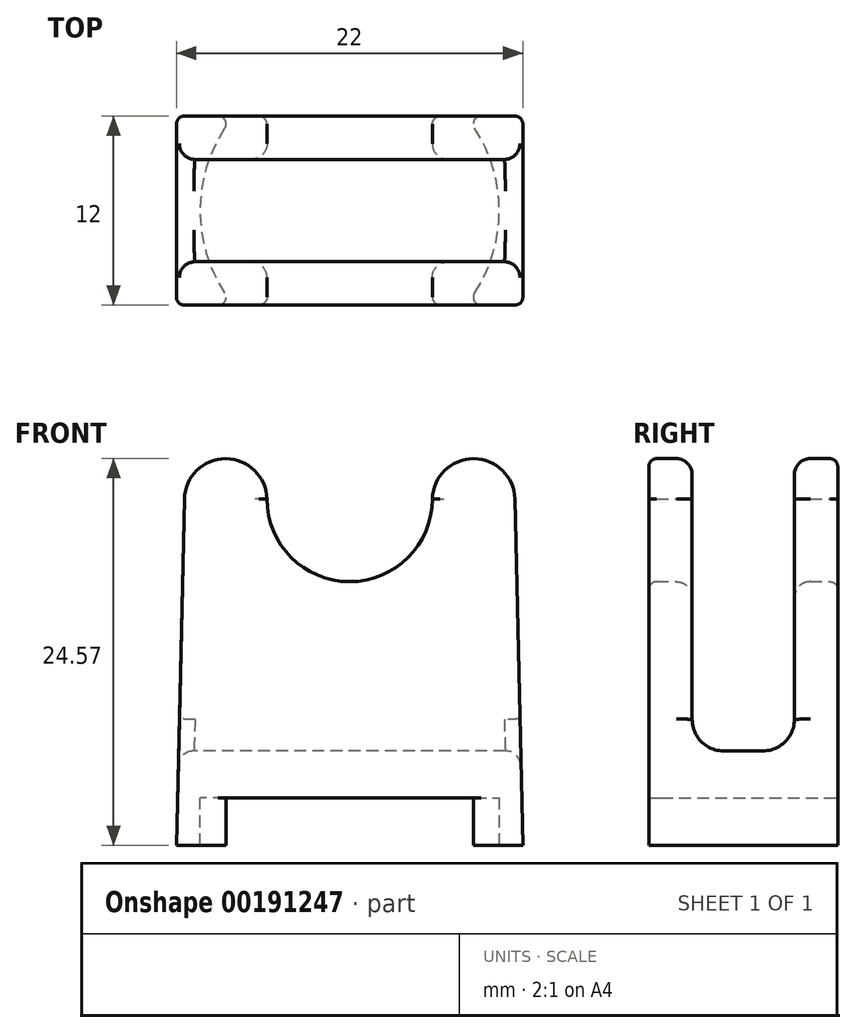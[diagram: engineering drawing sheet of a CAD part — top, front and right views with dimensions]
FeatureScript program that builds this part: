
annotation { "Feature Type Name" : "Feature", "Feature Type Description" : "" }
export const myFeature = defineFeature(function(context is Context, id is Id, definition is map)
    precondition{}
    {
        {
            var Q0;
            Q0=qCreatedBy(makeId("Front.planeOp"),FACE);
            var sketch = newSketch(context, id + "F0", { "sketchPlane" : qUnion([Q0])});
            skLineSegment(sketch, "E0", {"start": v(0, -3) * mm, "end": v(-11, -3) * mm});
            skLineSegment(sketch, "E1", {"start": v(-11, -3) * mm, "end": v(-10.5, 19) * mm});
            skLineSegment(sketch, "E2", {"start": v(-10.5, 19) * mm, "end": v(0, 19) * mm, "construction": true});
            skArc(sketch, "E3", {"start": v(-5.25, 19) * mm, "mid": v(0, 13.75) * mm, "end": v(5.25, 19) * mm});
            skArc(sketch, "E4", {"start": v(-10.5, 19) * mm, "mid": v(-7.87, 21.57) * mm, "end": v(-5.25, 19) * mm});
            skArc(sketch, "E5.MirrorCS", {"start": v(10.5, 19) * mm, "mid": v(7.87, 21.57) * mm, "end": v(5.25, 19) * mm});
            skLineSegment(sketch, "E6.MirrorCS", {"start": v(11, -3) * mm, "end": v(10.5, 19) * mm});
            skLineSegment(sketch, "E7.MirrorCS", {"start": v(0, -3) * mm, "end": v(11, -3) * mm});
            skSolve(sketch);
        }
        {
            var Q0;
            Q0=makeQuery(id+"F0.imprint","IMPRINT",FACE,{"disambiguationData":[TD([[makeQuery(id+"F0.imprint","IMPRINT",EDGE,{"derivedFrom":sQuery(id+"F0.wireOp",EDGE,"E0")}),-1.0]])]});
            extrude(context, id + "F1", {"entities" : qUnion([Q0]), "endBound" : BoundingType.SYMMETRIC, "depth" : 12 * mm});
        }
        {
            var Q0;
            Q0=qCreatedBy(makeId("Top.planeOp"),FACE);
            var sketch = newSketch(context, id + "F2", { "sketchPlane" : qUnion([Q0])});
            skCircle(sketch, "E8", {"center": v(0, 0) * mm, "radius": 9.5 * mm});
            skSolve(sketch);
        }
        {
            var Q0;
            Q0 = qSketchRegion(id + "F2", true);
            extrude(context, id + "F3", {"entities" : qUnion([Q0]), "operationType" : NewBodyOperationType.REMOVE, "oppositeDirection" : true, "depth" : 3 * mm});
        }
        {
            var Q0;
            Q0=qCreatedBy(makeId("Right.planeOp"),FACE);
            var sketch = newSketch(context, id + "F4", { "sketchPlane" : qUnion([Q0])});
            skLineSegment(sketch, "E9", {"start": v(0, 0) * mm, "end": v(0, 19) * mm, "construction": true});
            skLineSegment(sketch, "E10.bottom", {"start": v(3.25, 3) * mm, "end": v(-3.25, 3) * mm});
            skLineSegment(sketch, "E10.top", {"start": v(3.25, 35) * mm, "end": v(-3.25, 35) * mm});
            skLineSegment(sketch, "E10.left", {"start": v(3.25, 3) * mm, "end": v(3.25, 35) * mm});
            skLineSegment(sketch, "E10.right", {"start": v(-3.25, 3) * mm, "end": v(-3.25, 35) * mm});
            skPoint(sketch, "E10.middle", {"position": v(0, 19) * mm});
            skSolve(sketch);
        }
        {
            var Q0;
            Q0 = qSketchRegion(id + "F4", true);
            extrude(context, id + "F5", {"entities" : qUnion([Q0]), "operationType" : NewBodyOperationType.REMOVE, "endBound" : BoundingType.SYMMETRIC, "depth" : 22 * mm});
        }
        {
            var Q0;
            Q0=makeQuery(id+"F5.boolean.opBoolean","COPY",EDGE,{"derivedFrom":makeQuery(id+"F5.opExtrude","SWEPT_EDGE",EDGE,{"disambiguationData":[OSD([sQuery(id+"F4.wireOp",EDGE,"E10.bottom"),sQuery(id+"F4.wireOp",EDGE,"E10.left")])]})});
            var Q1;
            Q1=makeQuery(id+"F5.boolean.opBoolean","COPY",EDGE,{"derivedFrom":makeQuery(id+"F5.opExtrude","SWEPT_EDGE",EDGE,{"disambiguationData":[OSD([sQuery(id+"F4.wireOp",EDGE,"E10.bottom"),sQuery(id+"F4.wireOp",EDGE,"E10.right")])]})});
            fillet(context, id + "F6", {"entities" : qUnion([Q0, Q1]), "radius" : 2 * mm, "tangentPropagation" : true, "allowEdgeOverflow" : false});
        }
        {
            var Q0;
            Q0=makeQuery(id+"F5.boolean.opBoolean","INTERSECT",EDGE,{"derivedFrom":[makeQuery(id+"F1.opExtrude","SWEPT_FACE",FACE,{"disambiguationData":[OSD([sQuery(id+"F0.wireOp",EDGE,"E3")])]}),makeQuery(id+"F5.opExtrude","SWEPT_FACE",FACE,{"disambiguationData":[OSD([sQuery(id+"F4.wireOp",EDGE,"E10.left")])]})]});
            var Q1;
            Q1=makeQuery(id+"F5.boolean.opBoolean","INTERSECT",EDGE,{"derivedFrom":[makeQuery(id+"F1.opExtrude","SWEPT_FACE",FACE,{"disambiguationData":[OSD([sQuery(id+"F0.wireOp",EDGE,"E4")])]}),makeQuery(id+"F5.opExtrude","SWEPT_FACE",FACE,{"disambiguationData":[OSD([sQuery(id+"F4.wireOp",EDGE,"E10.left")])]})]});
            var Q2;
            Q2=makeQuery(id+"F5.boolean.opBoolean","INTERSECT",EDGE,{"derivedFrom":[makeQuery(id+"F1.opExtrude","SWEPT_FACE",FACE,{"disambiguationData":[OSD([sQuery(id+"F0.wireOp",EDGE,"E5.MirrorCS")])]}),makeQuery(id+"F5.opExtrude","SWEPT_FACE",FACE,{"disambiguationData":[OSD([sQuery(id+"F4.wireOp",EDGE,"E10.left")])]})]});
            var Q3;
            Q3=makeQuery(id+"F5.boolean.opBoolean","INTERSECT",EDGE,{"derivedFrom":[makeQuery(id+"F1.opExtrude","SWEPT_FACE",FACE,{"disambiguationData":[OSD([sQuery(id+"F0.wireOp",EDGE,"E1")])]}),makeQuery(id+"F5.opExtrude","SWEPT_FACE",FACE,{"disambiguationData":[OSD([sQuery(id+"F4.wireOp",EDGE,"E10.left")])]})]});
            var Q4;
            Q4=makeQuery(id+"F6.opFillet","BLEND_EDGE",EDGE,{"blendedFrom":[makeQuery(id+"F5.boolean.opBoolean","COPY",EDGE,{"derivedFrom":makeQuery(id+"F5.opExtrude","SWEPT_EDGE",EDGE,{"disambiguationData":[OSD([sQuery(id+"F4.wireOp",EDGE,"E10.bottom"),sQuery(id+"F4.wireOp",EDGE,"E10.left")])]})}),makeQuery(id+"F1.opExtrude","SWEPT_FACE",FACE,{"disambiguationData":[OSD([sQuery(id+"F0.wireOp",EDGE,"E1")])]})],"blendedInto":[makeQuery(id+"F1.opExtrude","SWEPT_FACE",FACE,{"disambiguationData":[OSD([sQuery(id+"F0.wireOp",EDGE,"E1")])]})]});
            var Q5;
            Q5=makeQuery(id+"F5.boolean.opBoolean","INTERSECT",EDGE,{"derivedFrom":[makeQuery(id+"F1.opExtrude","SWEPT_FACE",FACE,{"disambiguationData":[OSD([sQuery(id+"F0.wireOp",EDGE,"E1")])]}),makeQuery(id+"F5.opExtrude","SWEPT_FACE",FACE,{"disambiguationData":[OSD([sQuery(id+"F4.wireOp",EDGE,"E10.bottom")])]})]});
            var Q6;
            Q6=makeQuery(id+"F5.boolean.opBoolean","INTERSECT",EDGE,{"derivedFrom":[makeQuery(id+"F1.opExtrude","SWEPT_FACE",FACE,{"disambiguationData":[OSD([sQuery(id+"F0.wireOp",EDGE,"E1")])]}),makeQuery(id+"F5.opExtrude","SWEPT_FACE",FACE,{"disambiguationData":[OSD([sQuery(id+"F4.wireOp",EDGE,"E10.right")])]})]});
            var Q7;
            Q7=makeQuery(id+"F6.opFillet","BLEND_EDGE",EDGE,{"blendedFrom":[makeQuery(id+"F5.boolean.opBoolean","COPY",EDGE,{"derivedFrom":makeQuery(id+"F5.opExtrude","SWEPT_EDGE",EDGE,{"disambiguationData":[OSD([sQuery(id+"F4.wireOp",EDGE,"E10.bottom"),sQuery(id+"F4.wireOp",EDGE,"E10.right")])]})}),makeQuery(id+"F1.opExtrude","SWEPT_FACE",FACE,{"disambiguationData":[OSD([sQuery(id+"F0.wireOp",EDGE,"E1")])]})],"blendedInto":[makeQuery(id+"F1.opExtrude","SWEPT_FACE",FACE,{"disambiguationData":[OSD([sQuery(id+"F0.wireOp",EDGE,"E1")])]})]});
            var Q8;
            Q8=makeQuery(id+"F5.boolean.opBoolean","INTERSECT",EDGE,{"derivedFrom":[makeQuery(id+"F1.opExtrude","SWEPT_FACE",FACE,{"disambiguationData":[OSD([sQuery(id+"F0.wireOp",EDGE,"E4")])]}),makeQuery(id+"F5.opExtrude","SWEPT_FACE",FACE,{"disambiguationData":[OSD([sQuery(id+"F4.wireOp",EDGE,"E10.right")])]})]});
            var Q9;
            Q9=makeQuery(id+"F5.boolean.opBoolean","INTERSECT",EDGE,{"derivedFrom":[makeQuery(id+"F1.opExtrude","SWEPT_FACE",FACE,{"disambiguationData":[OSD([sQuery(id+"F0.wireOp",EDGE,"E3")])]}),makeQuery(id+"F5.opExtrude","SWEPT_FACE",FACE,{"disambiguationData":[OSD([sQuery(id+"F4.wireOp",EDGE,"E10.right")])]})]});
            var Q10;
            Q10=makeQuery(id+"F5.boolean.opBoolean","INTERSECT",EDGE,{"derivedFrom":[makeQuery(id+"F1.opExtrude","SWEPT_FACE",FACE,{"disambiguationData":[OSD([sQuery(id+"F0.wireOp",EDGE,"E5.MirrorCS")])]}),makeQuery(id+"F5.opExtrude","SWEPT_FACE",FACE,{"disambiguationData":[OSD([sQuery(id+"F4.wireOp",EDGE,"E10.right")])]})]});
            fillet(context, id + "F7", {"entities" : qUnion([Q0, Q1, Q2, Q3, Q4, Q5, Q6, Q7, Q8, Q9, Q10]), "radius" : 1 * mm, "tangentPropagation" : true, "allowEdgeOverflow" : false});
        }
        {
            var Q0;
            Q0=makeQuery(id+"F1.opExtrude","CAP_EDGE",EDGE,{"disambiguationData":[OSD([sQuery(id+"F0.wireOp",EDGE,"E1")])],"isStart":false});
            var Q1;
            Q1=makeQuery(id+"F1.opExtrude","CAP_EDGE",EDGE,{"disambiguationData":[OSD([sQuery(id+"F0.wireOp",EDGE,"E4")])],"isStart":false});
            var Q2;
            Q2=makeQuery(id+"F1.opExtrude","CAP_EDGE",EDGE,{"disambiguationData":[OSD([sQuery(id+"F0.wireOp",EDGE,"E3")])],"isStart":false});
            var Q3;
            Q3=makeQuery(id+"F1.opExtrude","CAP_EDGE",EDGE,{"disambiguationData":[OSD([sQuery(id+"F0.wireOp",EDGE,"E5.MirrorCS")])],"isStart":false});
            var Q4;
            Q4=makeQuery(id+"F3.boolean.opBoolean","INTERSECT",EDGE,{"disambiguationData":[OD(1.0)],"derivedFrom":[makeQuery(id+"F1.opExtrude","CAP_FACE",FACE,{"disambiguationData":[OSD([sQuery(id+"F0.wireOp",EDGE,"E0"),sQuery(id+"F0.wireOp",EDGE,"E1"),sQuery(id+"F0.wireOp",EDGE,"E3"),sQuery(id+"F0.wireOp",EDGE,"E4"),sQuery(id+"F0.wireOp",EDGE,"E5.MirrorCS"),sQuery(id+"F0.wireOp",EDGE,"E6.MirrorCS"),sQuery(id+"F0.wireOp",EDGE,"E7.MirrorCS")])],"isStart":false}),makeQuery(id+"F3.opExtrude","SWEPT_FACE",FACE,{"disambiguationData":[OSD([sQuery(id+"F2.wireOp",EDGE,"E8")])]})]});
            var Q5;
            Q5=makeQuery(id+"F3.boolean.opBoolean","INTERSECT",EDGE,{"disambiguationData":[OD(0.0)],"derivedFrom":[makeQuery(id+"F1.opExtrude","CAP_FACE",FACE,{"disambiguationData":[OSD([sQuery(id+"F0.wireOp",EDGE,"E0"),sQuery(id+"F0.wireOp",EDGE,"E1"),sQuery(id+"F0.wireOp",EDGE,"E3"),sQuery(id+"F0.wireOp",EDGE,"E4"),sQuery(id+"F0.wireOp",EDGE,"E5.MirrorCS"),sQuery(id+"F0.wireOp",EDGE,"E6.MirrorCS"),sQuery(id+"F0.wireOp",EDGE,"E7.MirrorCS")])],"isStart":false}),makeQuery(id+"F3.opExtrude","SWEPT_FACE",FACE,{"disambiguationData":[OSD([sQuery(id+"F2.wireOp",EDGE,"E8")])]})]});
            var Q6;
            Q6=makeQuery(id+"F1.opExtrude","CAP_EDGE",EDGE,{"disambiguationData":[OSD([sQuery(id+"F0.wireOp",EDGE,"E1")])],"isStart":true});
            var Q7;
            Q7=makeQuery(id+"F1.opExtrude","CAP_EDGE",EDGE,{"disambiguationData":[OSD([sQuery(id+"F0.wireOp",EDGE,"E4")])],"isStart":true});
            var Q8;
            Q8=makeQuery(id+"F1.opExtrude","CAP_EDGE",EDGE,{"disambiguationData":[OSD([sQuery(id+"F0.wireOp",EDGE,"E3")])],"isStart":true});
            var Q9;
            Q9=makeQuery(id+"F1.opExtrude","CAP_EDGE",EDGE,{"disambiguationData":[OSD([sQuery(id+"F0.wireOp",EDGE,"E5.MirrorCS")])],"isStart":true});
            var Q10;
            Q10=makeQuery(id+"F3.boolean.opBoolean","INTERSECT",EDGE,{"disambiguationData":[OD(1.0)],"derivedFrom":[makeQuery(id+"F1.opExtrude","CAP_FACE",FACE,{"disambiguationData":[OSD([sQuery(id+"F0.wireOp",EDGE,"E0"),sQuery(id+"F0.wireOp",EDGE,"E1"),sQuery(id+"F0.wireOp",EDGE,"E3"),sQuery(id+"F0.wireOp",EDGE,"E4"),sQuery(id+"F0.wireOp",EDGE,"E5.MirrorCS"),sQuery(id+"F0.wireOp",EDGE,"E6.MirrorCS"),sQuery(id+"F0.wireOp",EDGE,"E7.MirrorCS")])],"isStart":true}),makeQuery(id+"F3.opExtrude","SWEPT_FACE",FACE,{"disambiguationData":[OSD([sQuery(id+"F2.wireOp",EDGE,"E8")])]})]});
            var Q11;
            Q11=makeQuery(id+"F3.boolean.opBoolean","INTERSECT",EDGE,{"disambiguationData":[OD(0.0)],"derivedFrom":[makeQuery(id+"F1.opExtrude","CAP_FACE",FACE,{"disambiguationData":[OSD([sQuery(id+"F0.wireOp",EDGE,"E0"),sQuery(id+"F0.wireOp",EDGE,"E1"),sQuery(id+"F0.wireOp",EDGE,"E3"),sQuery(id+"F0.wireOp",EDGE,"E4"),sQuery(id+"F0.wireOp",EDGE,"E5.MirrorCS"),sQuery(id+"F0.wireOp",EDGE,"E6.MirrorCS"),sQuery(id+"F0.wireOp",EDGE,"E7.MirrorCS")])],"isStart":true}),makeQuery(id+"F3.opExtrude","SWEPT_FACE",FACE,{"disambiguationData":[OSD([sQuery(id+"F2.wireOp",EDGE,"E8")])]})]});
            fillet(context, id + "F8", {"entities" : qUnion([Q0, Q1, Q2, Q3, Q4, Q5, Q6, Q7, Q8, Q9, Q10, Q11]), "radius" : 0.5 * mm, "tangentPropagation" : true, "allowEdgeOverflow" : false});
        }
    });
